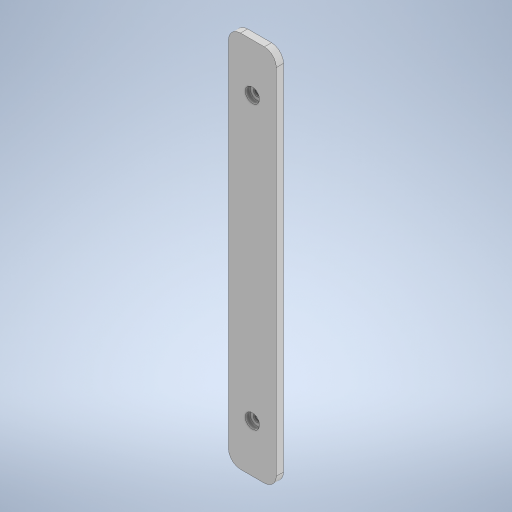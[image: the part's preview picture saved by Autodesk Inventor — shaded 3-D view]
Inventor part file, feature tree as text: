
AUTODESK INVENTOR PART (.ipt)
format: ipt  version: 2024.3 (Build 283343000, 343)  size: 263,680 bytes
history: native  units: mm
features: sketch x3, extrude x2, other x1, hole x1, fillet x1, projected_geometry x1
ambient origin geometry x8: Origin, YZ Plane, XZ Plane, XY Plane, X Axis, Y Axis, Z Axis, Center Point
bodies: Body1 (feature_tree)
feature tree (9):
  other  "ソリッド1"
  extrude  "押し出し1"  Depth=158.0mm
  hole  "穴1"  [1 undecoded]
  extrude  "押し出し2"  Depth=3.0mm TaperAngle=0.0deg
  fillet  "フィレット1"  Radius=20.0mm
  sketch  "スケッチ1"
  sketch  "スケッチ2"
  sketch  "スケッチ3"
  projected_geometry  "投影ループ1"
note: 1 required parameter value undecoded (feature->parameter linkage not recoverable at this tier; creation-order binding heuristic only, values carry confidence <= 0.55)
